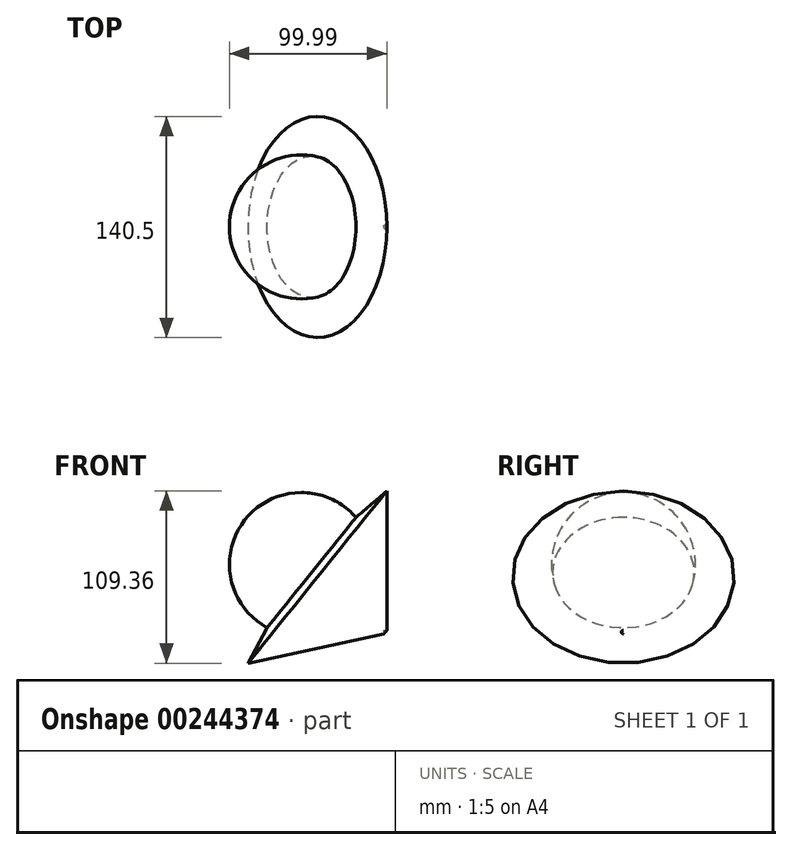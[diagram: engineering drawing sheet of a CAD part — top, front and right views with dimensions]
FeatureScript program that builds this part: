
annotation { "Feature Type Name" : "Feature", "Feature Type Description" : "" }
export const myFeature = defineFeature(function(context is Context, id is Id, definition is map)
    precondition{}
    {
        {
            var Q0;
            Q0=qCreatedBy(makeId("Front.planeOp"),FACE);
            var sketch = newSketch(context, id + "F0", { "sketchPlane" : qUnion([Q0])});
            skCircle(sketch, "E0", {"center": v(0, 0) * mm, "radius": 45.72 * mm});
            skLineSegment(sketch, "E1", {"start": v(0, 76.11) * mm, "end": v(0, -76.67) * mm});
            skSolve(sketch);
        }
        {
            var Q0;
            Q0=qCreatedBy(makeId("Front.planeOp"),FACE);
            var sketch = newSketch(context, id + "F1", { "sketchPlane" : qUnion([Q0])});
            skLineSegment(sketch, "E2", {"start": v(-55.77, 45.17) * mm, "end": v(52.1, -41.83) * mm});
            skLineSegment(sketch, "E3", {"start": v(-50.43, -42.83) * mm, "end": v(54.27, 46.67) * mm});
            skLineSegment(sketch, "E4", {"start": v(54.27, 46.67) * mm, "end": v(54.27, -41.83) * mm});
            skLineSegment(sketch, "E5", {"start": v(54.27, -41.83) * mm, "end": v(52.1, -41.83) * mm});
            skLineSegment(sketch, "E6", {"start": v(-50.43, -42.83) * mm, "end": v(-50.43, 45.17) * mm});
            skLineSegment(sketch, "E7", {"start": v(-50.43, 45.17) * mm, "end": v(-55.77, 45.17) * mm});
            skLineSegment(sketch, "E8", {"start": v(52.1, 44.81) * mm, "end": v(-50.43, 45.17) * mm});
            skLineSegment(sketch, "E9", {"start": v(52.1, -41.83) * mm, "end": v(-50.43, -41.83) * mm});
            skLineSegment(sketch, "E10", {"start": v(-50.43, -41.83) * mm, "end": v(-50.43, -42.83) * mm});
            skCircle(sketch, "E11", {"center": v(0, 0) * mm, "radius": 24.99 * mm});
            skSolve(sketch);
        }
        {
            var Q0;
            {var subQ0=sQuery(id+"F0.wireOp",EDGE,"E1");var subQ1=sQuery(id+"F0.wireOp",EDGE,"E0");var subQ2=makeQuery(id+"F0.imprint","INTERSECT",VERTEX,{"disambiguationData":[OD(0.0)],"derivedFrom":[subQ1,subQ0]});Q0=makeQuery(id+"F0.imprint","IMPRINT",FACE,{"disambiguationData":[TD([[makeQuery(id+"F0.imprint","IMPRINT",EDGE,{"disambiguationData":[TD([[subQ2,1.0]])],"derivedFrom":subQ1}),1.0]])]});}
            var Q1;
            Q1=sQuery(id+"F0.wireOp",EDGE,"E1");
            revolve(context, id + "F2", {"entities" : qUnion([Q0]), "axis" : qUnion([Q1]), "revolveType" : RevolveType.FULL});
        }
        {
            var Q0;
            {var subQ0=sQuery(id+"F1.wireOp",EDGE,"E4");Q0=makeQuery(id+"F1.imprint","IMPRINT",FACE,{"disambiguationData":[TD([[makeQuery(id+"F1.imprint","IMPRINT",EDGE,{"derivedFrom":subQ0}),-1.0]])]});}
            var Q1;
            Q1=sQuery(id+"F1.wireOp",EDGE,"E2");
            revolve(context, id + "F3", {"operationType" : NewBodyOperationType.ADD, "entities" : qUnion([Q0]), "axis" : qUnion([Q1]), "revolveType" : RevolveType.FULL});
        }
    });
